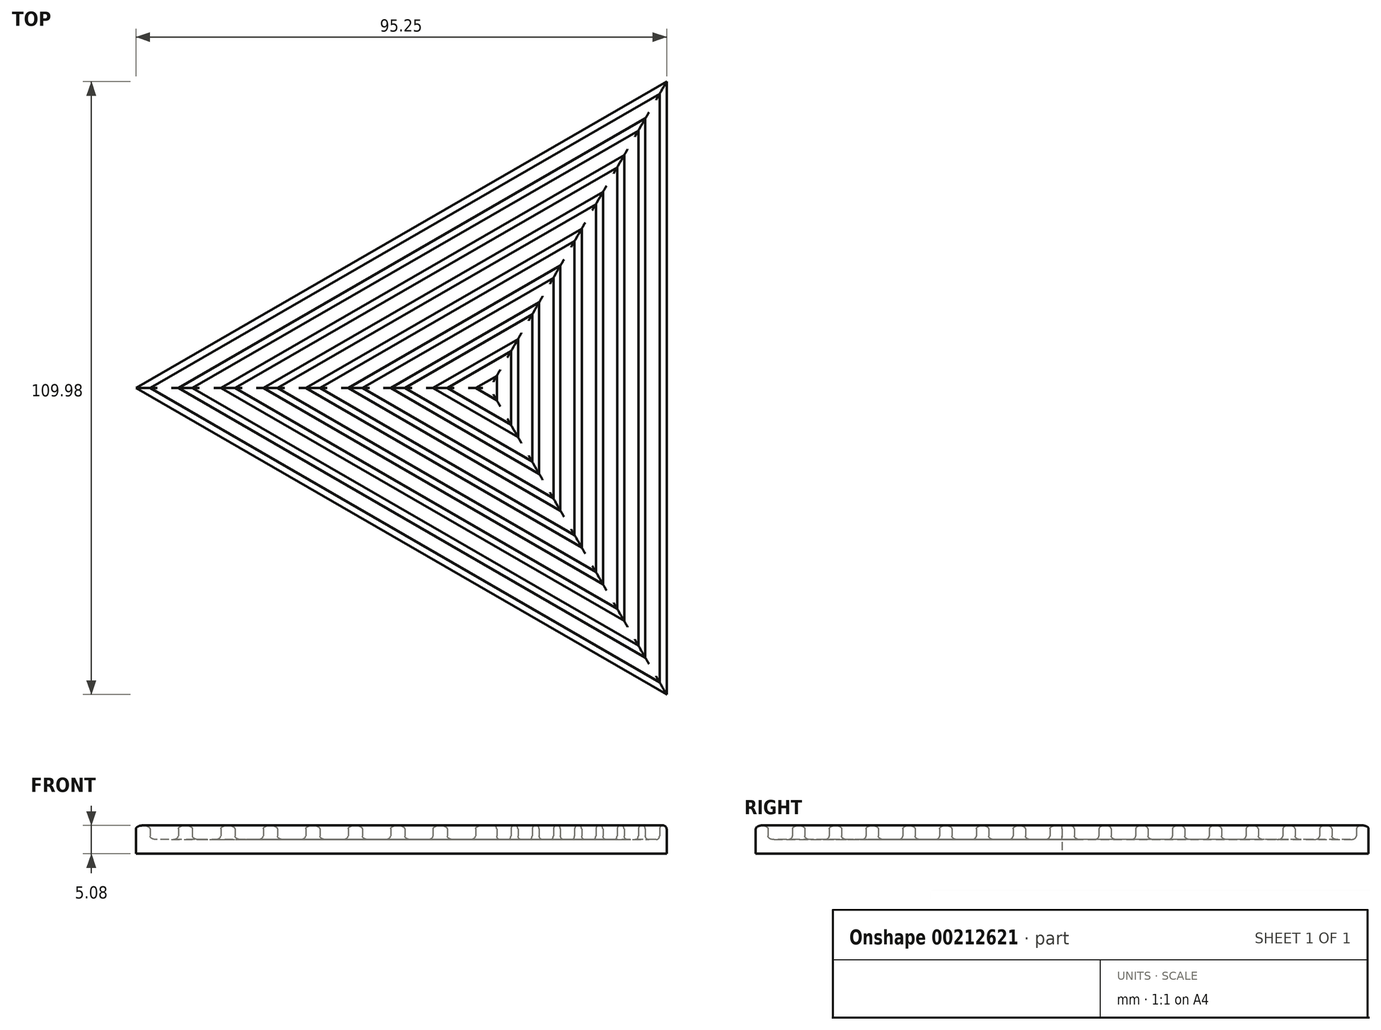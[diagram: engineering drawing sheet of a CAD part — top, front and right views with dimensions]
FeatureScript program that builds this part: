
annotation { "Feature Type Name" : "Feature", "Feature Type Description" : "" }
export const myFeature = defineFeature(function(context is Context, id is Id, definition is map)
    precondition{}
    {
        {
            var Q0;
            Q0=qCreatedBy(makeId("Top.planeOp"),FACE);
            var sketch = newSketch(context, id + "F0", { "sketchPlane" : qUnion([Q0])});
            skCircle(sketch, "E0", {"center": v(0, 0) * mm, "radius": 31.75 * mm});
            skLineSegment(sketch, "E1", {"start": v(31.75, 55) * mm, "end": v(-63.5, 0) * mm});
            skLineSegment(sketch, "E2", {"start": v(-63.5, 0) * mm, "end": v(31.75, -55) * mm});
            skLineSegment(sketch, "E3", {"start": v(31.75, -55) * mm, "end": v(31.75, 55) * mm});
            skSolve(sketch);
        }
        {
            var Q0;
            Q0 = qSketchRegion(id + "F0", true);
            extrude(context, id + "F1", {"entities" : qUnion([Q0]), "depth" : 2.54 * mm});
        }
        {
            var Q0;
            Q0=makeQuery(id+"F1.opExtrude","CAP_FACE",FACE,{"disambiguationData":[OSD([sQuery(id+"F0.wireOp",EDGE,"E1"),sQuery(id+"F0.wireOp",EDGE,"E2"),sQuery(id+"F0.wireOp",EDGE,"E3")])],"isStart":false});
            var sketch = newSketch(context, id + "F2", { "sketchPlane" : qUnion([Q0])});
            skLineSegment(sketch, "E4", {"start": v(-63.5, 0) * mm, "end": v(31.75, 55) * mm});
            skLineSegment(sketch, "E5", {"start": v(31.75, 55) * mm, "end": v(31.75, -55) * mm});
            skLineSegment(sketch, "E6", {"start": v(31.75, -55) * mm, "end": v(-63.5, 0) * mm});
            skLineSegment(sketch, "E7.0", {"start": v(-60.96, 0) * mm, "end": v(30.48, 52.8) * mm});
            skLineSegment(sketch, "E7.1", {"start": v(30.48, -52.8) * mm, "end": v(-60.96, 0) * mm});
            skLineSegment(sketch, "E7.2", {"start": v(30.48, 52.8) * mm, "end": v(30.48, -52.8) * mm});
            skLineSegment(sketch, "E8.0", {"start": v(-55.88, 0) * mm, "end": v(27.94, 48.4) * mm});
            skLineSegment(sketch, "E8.1", {"start": v(27.94, -48.4) * mm, "end": v(-55.88, 0) * mm});
            skLineSegment(sketch, "E8.2", {"start": v(27.94, 48.4) * mm, "end": v(27.94, -48.4) * mm});
            skLineSegment(sketch, "E9.0", {"start": v(26.67, 46.2) * mm, "end": v(26.67, -46.2) * mm});
            skLineSegment(sketch, "E9.1", {"start": v(-53.34, 0) * mm, "end": v(26.67, 46.2) * mm});
            skLineSegment(sketch, "E9.2", {"start": v(26.67, -46.2) * mm, "end": v(-53.34, 0) * mm});
            skLineSegment(sketch, "E10.0", {"start": v(-48.26, 0) * mm, "end": v(24.13, 41.8) * mm});
            skLineSegment(sketch, "E10.1", {"start": v(24.13, -41.8) * mm, "end": v(-48.26, 0) * mm});
            skLineSegment(sketch, "E10.2", {"start": v(24.13, 41.8) * mm, "end": v(24.13, -41.8) * mm});
            skLineSegment(sketch, "E11.0", {"start": v(-45.72, 0) * mm, "end": v(22.86, 39.6) * mm});
            skLineSegment(sketch, "E11.1", {"start": v(22.86, -39.6) * mm, "end": v(-45.72, 0) * mm});
            skLineSegment(sketch, "E11.2", {"start": v(22.86, 39.6) * mm, "end": v(22.86, -39.6) * mm});
            skLineSegment(sketch, "E12.0", {"start": v(-40.64, 0) * mm, "end": v(20.32, 35.2) * mm});
            skLineSegment(sketch, "E12.1", {"start": v(20.32, -35.2) * mm, "end": v(-40.64, 0) * mm});
            skLineSegment(sketch, "E12.2", {"start": v(20.32, 35.2) * mm, "end": v(20.32, -35.2) * mm});
            skLineSegment(sketch, "E13.0", {"start": v(-38.1, 0) * mm, "end": v(19.05, 33) * mm});
            skLineSegment(sketch, "E13.1", {"start": v(19.05, -33) * mm, "end": v(-38.1, 0) * mm});
            skLineSegment(sketch, "E13.2", {"start": v(19.05, 33) * mm, "end": v(19.05, -33) * mm});
            skLineSegment(sketch, "E14.0", {"start": v(-33.02, 0) * mm, "end": v(16.51, 28.6) * mm});
            skLineSegment(sketch, "E14.1", {"start": v(16.51, -28.6) * mm, "end": v(-33.02, 0) * mm});
            skLineSegment(sketch, "E14.2", {"start": v(16.51, 28.6) * mm, "end": v(16.51, -28.6) * mm});
            skLineSegment(sketch, "E15.0", {"start": v(-30.48, 0) * mm, "end": v(15.24, 26.4) * mm});
            skLineSegment(sketch, "E15.1", {"start": v(15.24, -26.4) * mm, "end": v(-30.48, 0) * mm});
            skLineSegment(sketch, "E15.2", {"start": v(15.24, 26.4) * mm, "end": v(15.24, -26.4) * mm});
            skLineSegment(sketch, "E16.0", {"start": v(-25.4, 0) * mm, "end": v(12.7, 22) * mm});
            skLineSegment(sketch, "E16.1", {"start": v(12.7, -22) * mm, "end": v(-25.4, 0) * mm});
            skLineSegment(sketch, "E16.2", {"start": v(12.7, 22) * mm, "end": v(12.7, -22) * mm});
            skLineSegment(sketch, "E17.0", {"start": v(11.43, 19.8) * mm, "end": v(11.43, -19.8) * mm});
            skLineSegment(sketch, "E17.1", {"start": v(-22.86, 0) * mm, "end": v(11.43, 19.8) * mm});
            skLineSegment(sketch, "E17.2", {"start": v(11.43, -19.8) * mm, "end": v(-22.86, 0) * mm});
            skLineSegment(sketch, "E18.0", {"start": v(8.9, 15.4) * mm, "end": v(8.9, -15.4) * mm});
            skLineSegment(sketch, "E18.1", {"start": v(-17.78, 0) * mm, "end": v(8.9, 15.4) * mm});
            skLineSegment(sketch, "E18.2", {"start": v(8.9, -15.4) * mm, "end": v(-17.78, 0) * mm});
            skLineSegment(sketch, "E19.0", {"start": v(7.62, 13.2) * mm, "end": v(7.62, -13.2) * mm});
            skLineSegment(sketch, "E19.1", {"start": v(-15.24, 0) * mm, "end": v(7.62, 13.2) * mm});
            skLineSegment(sketch, "E19.2", {"start": v(7.62, -13.2) * mm, "end": v(-15.24, 0) * mm});
            skLineSegment(sketch, "E20.0", {"start": v(5.08, 8.8) * mm, "end": v(5.08, -8.8) * mm});
            skLineSegment(sketch, "E20.1", {"start": v(-10.16, 0) * mm, "end": v(5.08, 8.8) * mm});
            skLineSegment(sketch, "E20.2", {"start": v(5.08, -8.8) * mm, "end": v(-10.16, 0) * mm});
            skLineSegment(sketch, "E21.0", {"start": v(-7.62, 0) * mm, "end": v(3.8, 6.6) * mm});
            skLineSegment(sketch, "E22.0", {"start": v(38.1, 66) * mm, "end": v(-76.2, 0) * mm});
            skLineSegment(sketch, "E22.1", {"start": v(38.1, -66) * mm, "end": v(38.1, 66) * mm});
            skLineSegment(sketch, "E22.2", {"start": v(-76.2, 0) * mm, "end": v(38.1, -66) * mm});
            skLineSegment(sketch, "E23.0", {"start": v(3.8, -6.6) * mm, "end": v(-7.62, 0) * mm});
            skLineSegment(sketch, "E24.trimOffspring", {"start": v(3.8, 6.6) * mm, "end": v(3.8, -6.6) * mm});
            skLineSegment(sketch, "E25", {"start": v(-2.54, 0) * mm, "end": v(1.27, -2.2) * mm});
            skLineSegment(sketch, "E26", {"start": v(1.27, -2.2) * mm, "end": v(1.27, 2.2) * mm});
            skLineSegment(sketch, "E27", {"start": v(1.27, 2.2) * mm, "end": v(-2.54, 0) * mm});
            skSolve(sketch);
        }
        {
            var Q0;
            Q0=makeQuery(id+"F2.imprint","IMPRINT",FACE,{"disambiguationData":[TD([[makeQuery(id+"F2.imprint","IMPRINT",EDGE,{"derivedFrom":sQuery(id+"F2.wireOp",EDGE,"E4")}),1.0]])]});
            var Q1;
            Q1=makeQuery(id+"F2.imprint","IMPRINT",FACE,{"disambiguationData":[TD([[makeQuery(id+"F2.imprint","IMPRINT",EDGE,{"derivedFrom":sQuery(id+"F2.wireOp",EDGE,"E8.0")}),-1.0]])]});
            var Q2;
            Q2=makeQuery(id+"F2.imprint","IMPRINT",FACE,{"disambiguationData":[TD([[makeQuery(id+"F2.imprint","IMPRINT",EDGE,{"derivedFrom":sQuery(id+"F2.wireOp",EDGE,"E10.0")}),-1.0]])]});
            var Q3;
            Q3=makeQuery(id+"F2.imprint","IMPRINT",FACE,{"disambiguationData":[TD([[makeQuery(id+"F2.imprint","IMPRINT",EDGE,{"derivedFrom":sQuery(id+"F2.wireOp",EDGE,"E12.0")}),-1.0]])]});
            var Q4;
            Q4=makeQuery(id+"F2.imprint","IMPRINT",FACE,{"disambiguationData":[TD([[makeQuery(id+"F2.imprint","IMPRINT",EDGE,{"derivedFrom":sQuery(id+"F2.wireOp",EDGE,"E14.0")}),-1.0]])]});
            var Q5;
            Q5=makeQuery(id+"F2.imprint","IMPRINT",FACE,{"disambiguationData":[TD([[makeQuery(id+"F2.imprint","IMPRINT",EDGE,{"derivedFrom":sQuery(id+"F2.wireOp",EDGE,"E16.0")}),-1.0]])]});
            var Q6;
            Q6=makeQuery(id+"F2.imprint","IMPRINT",FACE,{"disambiguationData":[TD([[makeQuery(id+"F2.imprint","IMPRINT",EDGE,{"derivedFrom":sQuery(id+"F2.wireOp",EDGE,"E18.0")}),-1.0]])]});
            var Q7;
            Q7=makeQuery(id+"F2.imprint","IMPRINT",FACE,{"disambiguationData":[TD([[makeQuery(id+"F2.imprint","IMPRINT",EDGE,{"derivedFrom":sQuery(id+"F2.wireOp",EDGE,"E20.0")}),-1.0]])]});
            var Q8;
            Q8=makeQuery(id+"F2.imprint","IMPRINT",FACE,{"disambiguationData":[TD([[makeQuery(id+"F2.imprint","IMPRINT",EDGE,{"derivedFrom":sQuery(id+"F2.wireOp",EDGE,"E25")}),1.0]])]});
            extrude(context, id + "F3", {"entities" : qUnion([Q0, Q1, Q2, Q3, Q4, Q5, Q6, Q7, Q8]), "operationType" : NewBodyOperationType.ADD, "depth" : 2.54 * mm});
        }
        {
            var Q0;
            Q0=makeQuery(id+"F3.opExtrude","CAP_FACE",FACE,{"disambiguationData":[OSD([sQuery(id+"F2.wireOp",EDGE,"E4"),sQuery(id+"F2.wireOp",EDGE,"E5"),sQuery(id+"F2.wireOp",EDGE,"E6"),sQuery(id+"F2.wireOp",EDGE,"E7.0"),sQuery(id+"F2.wireOp",EDGE,"E7.1"),sQuery(id+"F2.wireOp",EDGE,"E7.2")])],"isStart":false});
            var Q1;
            Q1=makeQuery(id+"F3.boolean.opBoolean","SPLIT",FACE,{"disambiguationData":[TD([makeQuery(id+"F3.opExtrude","SWEPT_FACE",FACE,{"disambiguationData":[OSD([sQuery(id+"F2.wireOp",EDGE,"E7.0")])]})])],"derivedFrom":makeQuery(id+"F1.opExtrude","CAP_FACE",FACE,{"disambiguationData":[OSD([sQuery(id+"F0.wireOp",EDGE,"E1"),sQuery(id+"F0.wireOp",EDGE,"E2"),sQuery(id+"F0.wireOp",EDGE,"E3")])],"isStart":false})});
            var Q2;
            Q2=makeQuery(id+"F3.opExtrude","CAP_FACE",FACE,{"disambiguationData":[OSD([sQuery(id+"F2.wireOp",EDGE,"E8.0"),sQuery(id+"F2.wireOp",EDGE,"E8.1"),sQuery(id+"F2.wireOp",EDGE,"E8.2"),sQuery(id+"F2.wireOp",EDGE,"E9.0"),sQuery(id+"F2.wireOp",EDGE,"E9.1"),sQuery(id+"F2.wireOp",EDGE,"E9.2")])],"isStart":false});
            var Q3;
            Q3=makeQuery(id+"F3.boolean.opBoolean","SPLIT",FACE,{"disambiguationData":[TD([makeQuery(id+"F3.opExtrude","SWEPT_FACE",FACE,{"disambiguationData":[OSD([sQuery(id+"F2.wireOp",EDGE,"E9.0")])]})])],"derivedFrom":makeQuery(id+"F1.opExtrude","CAP_FACE",FACE,{"disambiguationData":[OSD([sQuery(id+"F0.wireOp",EDGE,"E1"),sQuery(id+"F0.wireOp",EDGE,"E2"),sQuery(id+"F0.wireOp",EDGE,"E3")])],"isStart":false})});
            var Q4;
            Q4=makeQuery(id+"F3.opExtrude","CAP_FACE",FACE,{"disambiguationData":[OSD([sQuery(id+"F2.wireOp",EDGE,"E10.0"),sQuery(id+"F2.wireOp",EDGE,"E10.1"),sQuery(id+"F2.wireOp",EDGE,"E10.2"),sQuery(id+"F2.wireOp",EDGE,"E11.0"),sQuery(id+"F2.wireOp",EDGE,"E11.1"),sQuery(id+"F2.wireOp",EDGE,"E11.2")])],"isStart":false});
            var Q5;
            Q5=makeQuery(id+"F3.boolean.opBoolean","SPLIT",FACE,{"disambiguationData":[TD([makeQuery(id+"F3.opExtrude","SWEPT_FACE",FACE,{"disambiguationData":[OSD([sQuery(id+"F2.wireOp",EDGE,"E11.0")])]})])],"derivedFrom":makeQuery(id+"F1.opExtrude","CAP_FACE",FACE,{"disambiguationData":[OSD([sQuery(id+"F0.wireOp",EDGE,"E1"),sQuery(id+"F0.wireOp",EDGE,"E2"),sQuery(id+"F0.wireOp",EDGE,"E3")])],"isStart":false})});
            var Q6;
            Q6=makeQuery(id+"F3.opExtrude","CAP_FACE",FACE,{"disambiguationData":[OSD([sQuery(id+"F2.wireOp",EDGE,"E12.0"),sQuery(id+"F2.wireOp",EDGE,"E12.1"),sQuery(id+"F2.wireOp",EDGE,"E12.2"),sQuery(id+"F2.wireOp",EDGE,"E13.0"),sQuery(id+"F2.wireOp",EDGE,"E13.1"),sQuery(id+"F2.wireOp",EDGE,"E13.2")])],"isStart":false});
            var Q7;
            Q7=makeQuery(id+"F3.boolean.opBoolean","SPLIT",FACE,{"disambiguationData":[TD([makeQuery(id+"F3.opExtrude","SWEPT_FACE",FACE,{"disambiguationData":[OSD([sQuery(id+"F2.wireOp",EDGE,"E13.0")])]})])],"derivedFrom":makeQuery(id+"F1.opExtrude","CAP_FACE",FACE,{"disambiguationData":[OSD([sQuery(id+"F0.wireOp",EDGE,"E1"),sQuery(id+"F0.wireOp",EDGE,"E2"),sQuery(id+"F0.wireOp",EDGE,"E3")])],"isStart":false})});
            var Q8;
            Q8=makeQuery(id+"F3.opExtrude","CAP_FACE",FACE,{"disambiguationData":[OSD([sQuery(id+"F2.wireOp",EDGE,"E14.0"),sQuery(id+"F2.wireOp",EDGE,"E14.1"),sQuery(id+"F2.wireOp",EDGE,"E14.2"),sQuery(id+"F2.wireOp",EDGE,"E15.0"),sQuery(id+"F2.wireOp",EDGE,"E15.1"),sQuery(id+"F2.wireOp",EDGE,"E15.2")])],"isStart":false});
            var Q9;
            Q9=makeQuery(id+"F3.boolean.opBoolean","SPLIT",FACE,{"disambiguationData":[TD([makeQuery(id+"F3.opExtrude","SWEPT_FACE",FACE,{"disambiguationData":[OSD([sQuery(id+"F2.wireOp",EDGE,"E15.0")])]})])],"derivedFrom":makeQuery(id+"F1.opExtrude","CAP_FACE",FACE,{"disambiguationData":[OSD([sQuery(id+"F0.wireOp",EDGE,"E1"),sQuery(id+"F0.wireOp",EDGE,"E2"),sQuery(id+"F0.wireOp",EDGE,"E3")])],"isStart":false})});
            var Q10;
            Q10=makeQuery(id+"F3.opExtrude","CAP_FACE",FACE,{"disambiguationData":[OSD([sQuery(id+"F2.wireOp",EDGE,"E16.0"),sQuery(id+"F2.wireOp",EDGE,"E16.1"),sQuery(id+"F2.wireOp",EDGE,"E16.2"),sQuery(id+"F2.wireOp",EDGE,"E17.0"),sQuery(id+"F2.wireOp",EDGE,"E17.1"),sQuery(id+"F2.wireOp",EDGE,"E17.2")])],"isStart":false});
            var Q11;
            Q11=makeQuery(id+"F3.boolean.opBoolean","SPLIT",FACE,{"disambiguationData":[TD([makeQuery(id+"F3.opExtrude","SWEPT_FACE",FACE,{"disambiguationData":[OSD([sQuery(id+"F2.wireOp",EDGE,"E17.0")])]})])],"derivedFrom":makeQuery(id+"F1.opExtrude","CAP_FACE",FACE,{"disambiguationData":[OSD([sQuery(id+"F0.wireOp",EDGE,"E1"),sQuery(id+"F0.wireOp",EDGE,"E2"),sQuery(id+"F0.wireOp",EDGE,"E3")])],"isStart":false})});
            var Q12;
            Q12=makeQuery(id+"F3.opExtrude","CAP_FACE",FACE,{"disambiguationData":[OSD([sQuery(id+"F2.wireOp",EDGE,"E18.0"),sQuery(id+"F2.wireOp",EDGE,"E18.1"),sQuery(id+"F2.wireOp",EDGE,"E18.2"),sQuery(id+"F2.wireOp",EDGE,"E19.0"),sQuery(id+"F2.wireOp",EDGE,"E19.1"),sQuery(id+"F2.wireOp",EDGE,"E19.2")])],"isStart":false});
            var Q13;
            Q13=makeQuery(id+"F3.boolean.opBoolean","SPLIT",FACE,{"disambiguationData":[TD([makeQuery(id+"F3.opExtrude","SWEPT_FACE",FACE,{"disambiguationData":[OSD([sQuery(id+"F2.wireOp",EDGE,"E19.0")])]})])],"derivedFrom":makeQuery(id+"F1.opExtrude","CAP_FACE",FACE,{"disambiguationData":[OSD([sQuery(id+"F0.wireOp",EDGE,"E1"),sQuery(id+"F0.wireOp",EDGE,"E2"),sQuery(id+"F0.wireOp",EDGE,"E3")])],"isStart":false})});
            var Q14;
            Q14=makeQuery(id+"F3.opExtrude","CAP_FACE",FACE,{"disambiguationData":[OSD([sQuery(id+"F2.wireOp",EDGE,"E20.0"),sQuery(id+"F2.wireOp",EDGE,"E20.1"),sQuery(id+"F2.wireOp",EDGE,"E20.2"),sQuery(id+"F2.wireOp",EDGE,"E21.0"),sQuery(id+"F2.wireOp",EDGE,"E23.0"),sQuery(id+"F2.wireOp",EDGE,"E24.trimOffspring")])],"isStart":false});
            var Q15;
            Q15=makeQuery(id+"F3.boolean.opBoolean","SPLIT",FACE,{"disambiguationData":[TD([makeQuery(id+"F3.opExtrude","SWEPT_FACE",FACE,{"disambiguationData":[OSD([sQuery(id+"F2.wireOp",EDGE,"E21.0")])]})])],"derivedFrom":makeQuery(id+"F1.opExtrude","CAP_FACE",FACE,{"disambiguationData":[OSD([sQuery(id+"F0.wireOp",EDGE,"E1"),sQuery(id+"F0.wireOp",EDGE,"E2"),sQuery(id+"F0.wireOp",EDGE,"E3")])],"isStart":false})});
            var Q16;
            Q16=makeQuery(id+"F3.opExtrude","CAP_FACE",FACE,{"disambiguationData":[OSD([sQuery(id+"F2.wireOp",EDGE,"E25"),sQuery(id+"F2.wireOp",EDGE,"E26"),sQuery(id+"F2.wireOp",EDGE,"E27")])],"isStart":false});
            fillet(context, id + "F4", {"entities" : qUnion([Q0, Q1, Q2, Q3, Q4, Q5, Q6, Q7, Q8, Q9, Q10, Q11, Q12, Q13, Q14, Q15, Q16]), "radius" : 0.64 * mm, "tangentPropagation" : true, "allowEdgeOverflow" : false});
        }
    });
